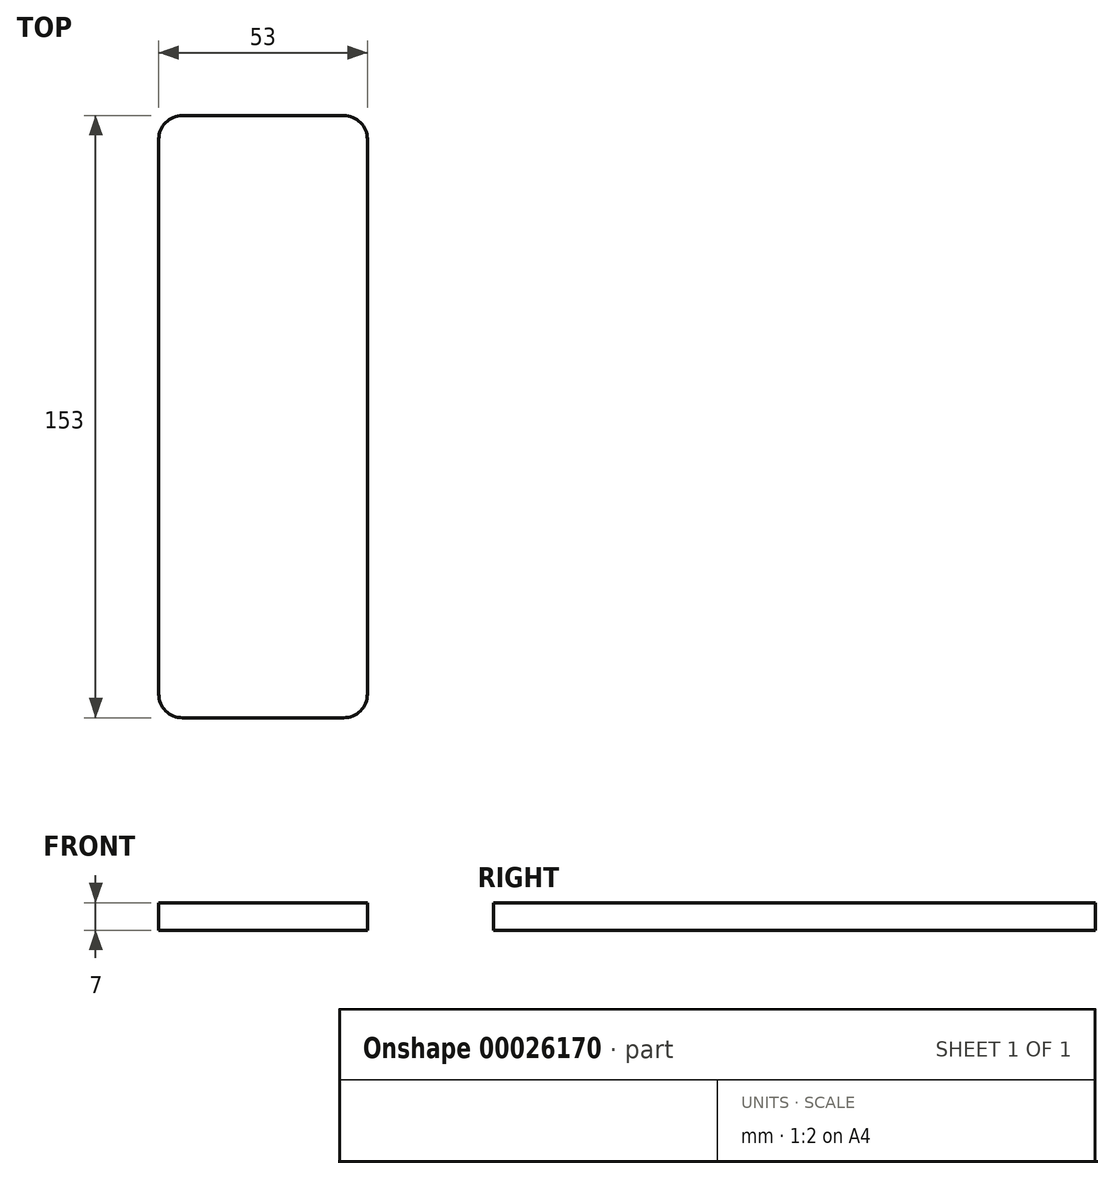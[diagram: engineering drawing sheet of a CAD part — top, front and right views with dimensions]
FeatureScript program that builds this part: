
annotation { "Feature Type Name" : "Feature", "Feature Type Description" : "" }
export const myFeature = defineFeature(function(context is Context, id is Id, definition is map)
    precondition{}
    {
        {
            var Q0;
            Q0=qCreatedBy(makeId("Top.planeOp"),FACE);
            var sketch = newSketch(context, id + "F0", { "sketchPlane" : qUnion([Q0])});
            skLineSegment(sketch, "E0.rect.bottom", {"start": v(-49.77, 32.92) * mm, "end": v(-102.77, 32.92) * mm});
            skLineSegment(sketch, "E0.rect.top", {"start": v(-49.77, -120.08) * mm, "end": v(-102.77, -120.08) * mm});
            skLineSegment(sketch, "E0.rect.left", {"start": v(-49.77, 32.92) * mm, "end": v(-49.77, -120.08) * mm});
            skLineSegment(sketch, "E0.rect.right", {"start": v(-102.77, 32.92) * mm, "end": v(-102.77, -120.08) * mm});
            skPoint(sketch, "E0.rect.middle", {"position": v(-76.27, -43.58) * mm});
            skSolve(sketch);
        }
        {
            var Q0;
            Q0=makeQuery(id+"F0.imprint","IMPRINT",FACE,{"disambiguationData":[TD([[makeQuery(id+"F0.imprint","IMPRINT",EDGE,{"derivedFrom":sQuery(id+"F0.wireOp",EDGE,"E0.rect.bottom")}),1.0]])]});
            extrude(context, id + "F1", {"entities" : qUnion([Q0]), "depth" : 7 * mm});
        }
        {
            var Q0;
            Q0=makeQuery(id+"F1.opExtrude","SWEPT_EDGE",EDGE,{"disambiguationData":[OSD([sQuery(id+"F0.wireOp",EDGE,"E0.rect.top"),sQuery(id+"F0.wireOp",EDGE,"E0.rect.left")])]});
            var Q1;
            Q1=makeQuery(id+"F1.opExtrude","SWEPT_EDGE",EDGE,{"disambiguationData":[OSD([sQuery(id+"F0.wireOp",EDGE,"E0.rect.top"),sQuery(id+"F0.wireOp",EDGE,"E0.rect.right")])]});
            var Q2;
            Q2=makeQuery(id+"F1.opExtrude","SWEPT_EDGE",EDGE,{"disambiguationData":[OSD([sQuery(id+"F0.wireOp",EDGE,"E0.rect.bottom"),sQuery(id+"F0.wireOp",EDGE,"E0.rect.left")])]});
            var Q3;
            Q3=makeQuery(id+"F1.opExtrude","SWEPT_EDGE",EDGE,{"disambiguationData":[OSD([sQuery(id+"F0.wireOp",EDGE,"E0.rect.bottom"),sQuery(id+"F0.wireOp",EDGE,"E0.rect.right")])]});
            fillet(context, id + "F2", {"entities" : qUnion([Q0, Q1, Q2, Q3]), "radius" : 6 * mm, "tangentPropagation" : true, "allowEdgeOverflow" : false});
        }
    });
